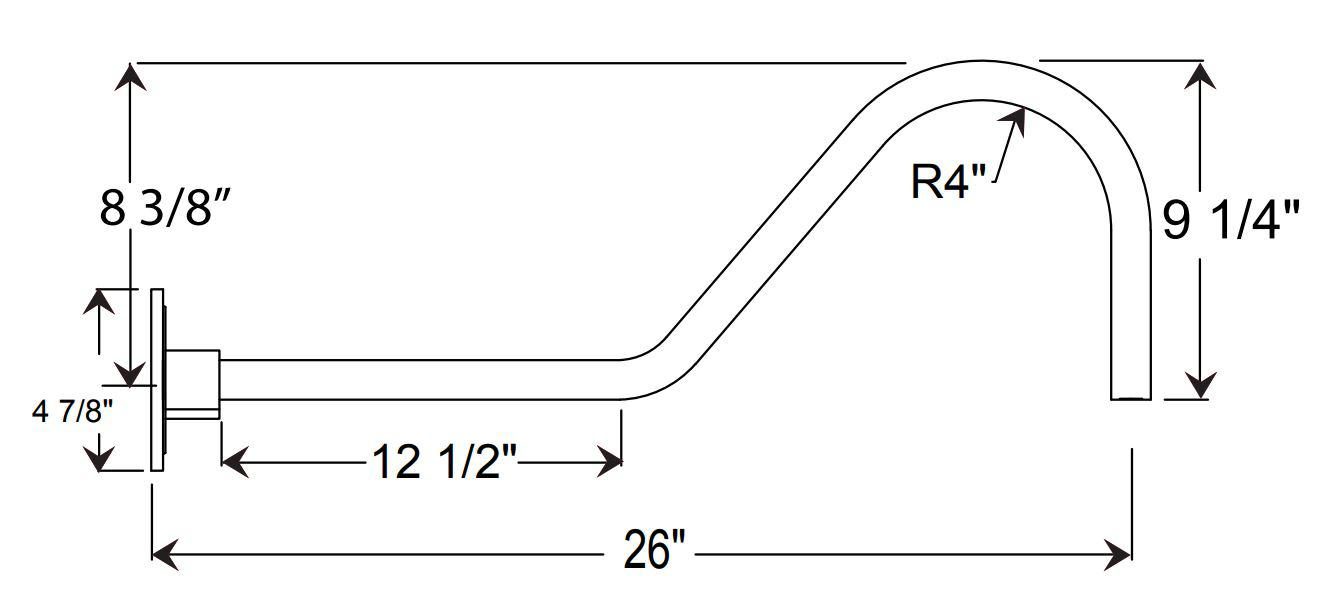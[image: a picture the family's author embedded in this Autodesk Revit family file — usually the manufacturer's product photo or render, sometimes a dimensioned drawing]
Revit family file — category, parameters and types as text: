
# Revit family: GUP120 - 6,7
name_source: partatom
category: Lighting Fixtures
units: mm (PartAtom-declared; Revit-internal decimal feet)

## family parameters
Always vertical = Yes
Cut with Voids When Loaded = No
Light Source = Yes
OmniClass Number = 23.80.70.00
OmniClass Title = Lighting
Part Type = Normal
Room Calculation Point = No
Round Connector Dimension = Use Diameter
Shared = No
Work Plane-Based = No

## types (2) — shared parameters
Apparent Load = 200 VA
Body Material = body
Color Filter = 16777215
Construction Material = Cast aluminum.
Default Elevation = 0' - 0"
Description = 120-277 Voltage
Dimming Lamp Color Temperature Shift = <None>
Fixture Height = 0' - 10 1/2"
Lamp = Incandescent Wire Lamp
Load Classification = Lighting
Manufacturer = ANP Lighting
Photometric Web File = generic.ies
Power Factor = 1
Tilt Angle = 90.00°
URL = https://www.anplighting.com
Voltage = 277 V
Warranty = 5 year limited warranty
Wattage Comments = 200W Max
Weight = 2 lbs

## per-type parameters (varying)
| type | Fixture Diameter | GUP120-6" | GUP120-7" | Model |
| GUP110-6" | 0' - 6" | Yes | No | GUP120-6" |
| GUP110-7" | 0' - 7" | No | Yes | GUP120-7" |

## geometry (parser evidence)
native form markers: Sweep x30
no freeform markers — native parametric forms only
